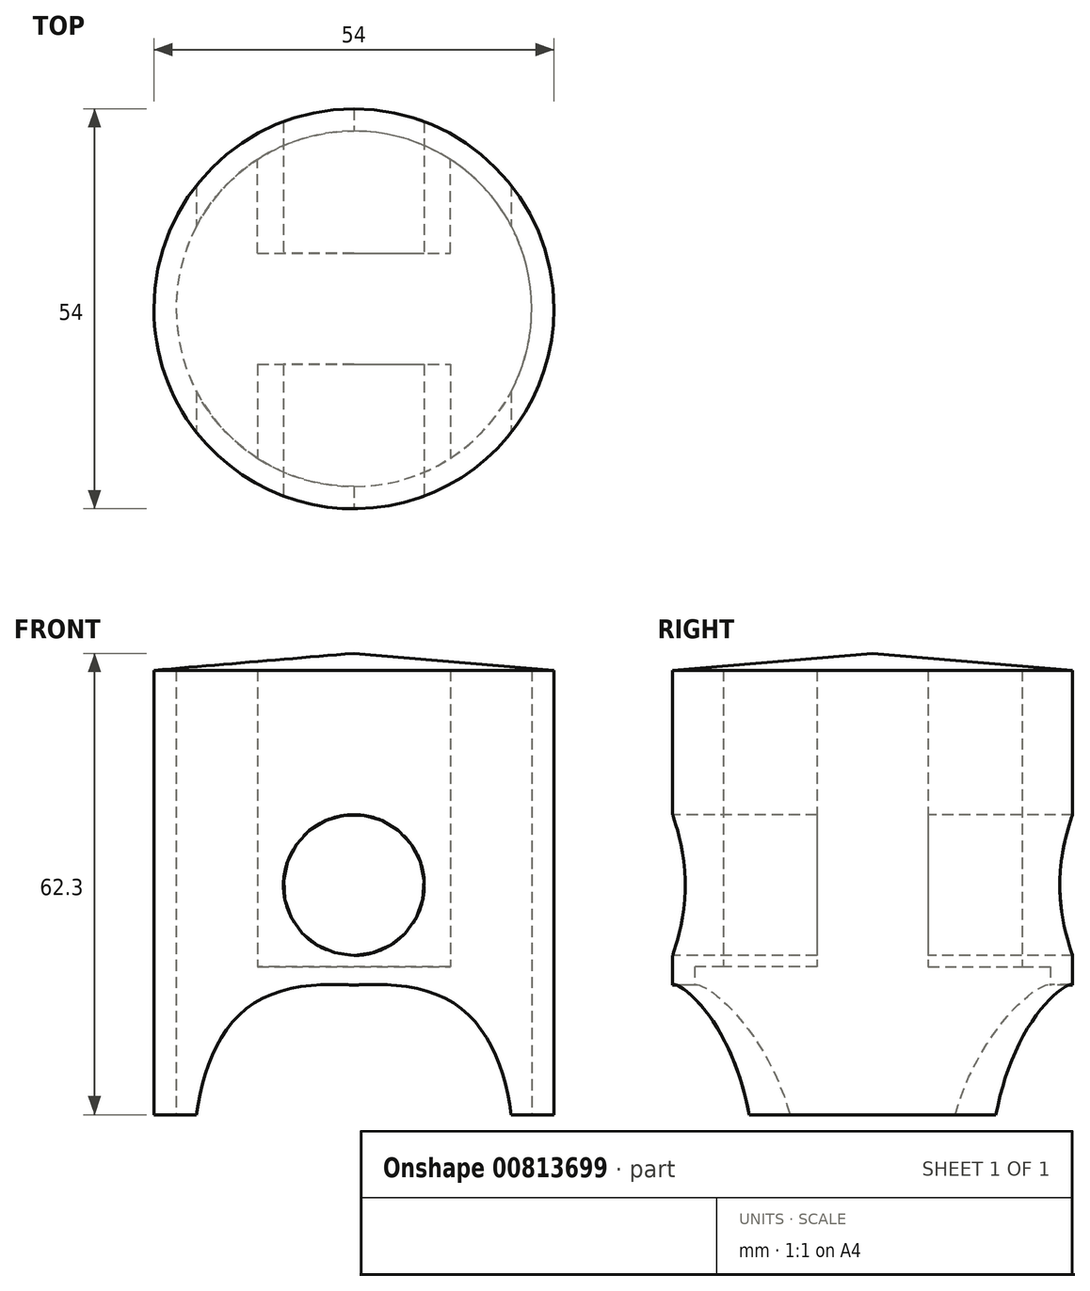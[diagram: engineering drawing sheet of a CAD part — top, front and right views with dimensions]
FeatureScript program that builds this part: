
annotation { "Feature Type Name" : "Feature", "Feature Type Description" : "" }
export const myFeature = defineFeature(function(context is Context, id is Id, definition is map)
    precondition{}
    {
        {
            var Q0;
            Q0=qCreatedBy(makeId("Top.planeOp"),FACE);
            var sketch = newSketch(context, id + "F0", { "sketchPlane" : qUnion([Q0])});
            skCircle(sketch, "E0", {"center": v(0, 0) * mm, "radius": 27 * mm});
            skLineSegment(sketch, "E1", {"start": v(-13, 7.5) * mm, "end": v(13, 7.5) * mm});
            skLineSegment(sketch, "E2", {"start": v(-13, 7.5) * mm, "end": v(-13, 20.17) * mm});
            skLineSegment(sketch, "E3", {"start": v(13, 7.5) * mm, "end": v(13, 20.17) * mm});
            skLineSegment(sketch, "E4.MirrorCS", {"start": v(-13, -7.5) * mm, "end": v(-13, -20.17) * mm});
            skLineSegment(sketch, "E5.MirrorCS", {"start": v(-13, -7.5) * mm, "end": v(13, -7.5) * mm});
            skLineSegment(sketch, "E6.MirrorCS", {"start": v(13, -7.5) * mm, "end": v(13, -20.17) * mm});
            skCircle(sketch, "E7", {"center": v(0, 0) * mm, "radius": 24 * mm});
            skSolve(sketch);
        }
        {
            var Q0;
            Q0=makeQuery(id+"F0.imprint","IMPRINT",FACE,{"disambiguationData":[TD([[makeQuery(id+"F0.imprint","IMPRINT",EDGE,{"derivedFrom":sQuery(id+"F0.wireOp",EDGE,"E0")}),1.0]])]});
            extrude(context, id + "F1", {"entities" : qUnion([Q0]), "depth" : 40 * mm, "offsetDistance" : 25 * mm, "hasSecondDirection" : true, "secondDirectionOppositeDirection" : true, "secondDirectionDepth" : 20 * mm});
        }
        {
            var Q0;
            Q0 = qSketchRegion(id + "F0", true);
            var Q1;
            Q1=makeQuery(id+"F0.imprint","IMPRINT",FACE,{"disambiguationData":[TD([[makeQuery(id+"F0.imprint","IMPRINT",EDGE,{"derivedFrom":sQuery(id+"F0.wireOp",EDGE,"E1")}),1.0]])]});
            extrude(context, id + "F2", {"entities" : qUnion([Q0, Q1]), "operationType" : NewBodyOperationType.ADD, "depth" : 40 * mm, "offsetDistance" : 25 * mm, "hasSecondDirection" : true, "secondDirectionOppositeDirection" : true, "secondDirectionDepth" : 0 * mm});
        }
        {
            var Q0;
            Q0 = qSketchRegion(id + "F0", true);
            var Q1;
            {var subQ0=sQuery(id+"F0.wireOp",EDGE,"E4.MirrorCS");Q1=makeQuery(id+"F0.imprint","IMPRINT",FACE,{"disambiguationData":[TD([[makeQuery(id+"F0.imprint","IMPRINT",EDGE,{"derivedFrom":subQ0}),1.0]])]});}
            extrude(context, id + "F3", {"entities" : qUnion([Q0, Q1]), "operationType" : NewBodyOperationType.ADD, "depth" : 40 * mm, "offsetDistance" : 25 * mm, "hasSecondDirection" : true, "secondDirectionOppositeDirection" : true, "secondDirectionDepth" : 0 * mm});
        }
        {
            var Q0;
            Q0=qCreatedBy(makeId("Front.planeOp"),FACE);
            var sketch = newSketch(context, id + "F4", { "sketchPlane" : qUnion([Q0])});
            skLineSegment(sketch, "E8", {"start": v(-21.25, -20) * mm, "end": v(21.25, -20) * mm});
            skLineSegment(sketch, "E9", {"start": v(0, 0) * mm, "end": v(0, 0) * mm});
            skFitSpline(sketch, "E10", {"points": [v(-21.25, -20) * mm, v(0, -2.5) * mm], "startDerivative": vector(6.92, 47.7) * mm, "endDerivative": vector(30.91, -1.87) * mm});
            skFitSpline(sketch, "E11.MirrorCS", {"points": [v(21.25, -20) * mm, v(0, -2.5) * mm], "startDerivative": vector(-6.92, 47.7) * mm, "endDerivative": vector(-30.91, -1.87) * mm});
            skSolve(sketch);
        }
        {
            var Q0;
            Q0=qSketchRegion(id+"F4",true);
            extrude(context, id + "F5", {"entities" : qUnion([Q0]), "operationType" : NewBodyOperationType.REMOVE, "oppositeDirection" : true, "depth" : 30 * mm, "offsetDistance" : 25 * mm, "hasSecondDirection" : true, "secondDirectionOppositeDirection" : false, "secondDirectionDepth" : 30 * mm});
        }
        {
            var Q0;
            Q0=qCreatedBy(makeId("Front.planeOp"),FACE);
            var sketch = newSketch(context, id + "F6", { "sketchPlane" : qUnion([Q0])});
            skLineSegment(sketch, "E12", {"start": v(0, 0) * mm, "end": v(0, 11) * mm});
            skCircle(sketch, "E13", {"center": v(0, 11) * mm, "radius": 9.5 * mm});
            skSolve(sketch);
        }
        {
            var Q0;
            Q0=qSketchRegion(id+"F6",true);
            extrude(context, id + "F7", {"entities" : qUnion([Q0]), "operationType" : NewBodyOperationType.REMOVE, "oppositeDirection" : true, "depth" : 30 * mm, "offsetDistance" : 25 * mm, "hasSecondDirection" : true, "secondDirectionOppositeDirection" : false, "secondDirectionDepth" : 30 * mm});
        }
        {
            var Q0;
            Q0=qCreatedBy(makeId("Front.planeOp"),FACE);
            var sketch = newSketch(context, id + "F8", { "sketchPlane" : qUnion([Q0])});
            skLineSegment(sketch, "E14", {"start": v(0, 40) * mm, "end": v(0, 0) * mm, "construction": true});
            skLineSegment(sketch, "E15", {"start": v(0, 40) * mm, "end": v(0, 42.3) * mm});
            skLineSegment(sketch, "E16", {"start": v(0, 40) * mm, "end": v(-27, 40) * mm});
            skLineSegment(sketch, "E17", {"start": v(-27, 40) * mm, "end": v(0, 42.3) * mm});
            skSolve(sketch);
        }
        {
            var Q0;
            Q0=makeQuery(id+"F8.imprint","IMPRINT",FACE,{"disambiguationData":[TD([[makeQuery(id+"F8.imprint","IMPRINT",EDGE,{"derivedFrom":sQuery(id+"F8.wireOp",EDGE,"E15")}),1.0]])]});
            var Q1;
            Q1=sQuery(id+"F8.wireOp",EDGE,"E15");
            revolve(context, id + "F9", {"operationType" : NewBodyOperationType.ADD, "surfaceOperationType" : NewSurfaceOperationType.NEW, "entities" : qUnion([Q0]), "axis" : qUnion([Q1]), "revolveType" : RevolveType.FULL});
        }
    });
